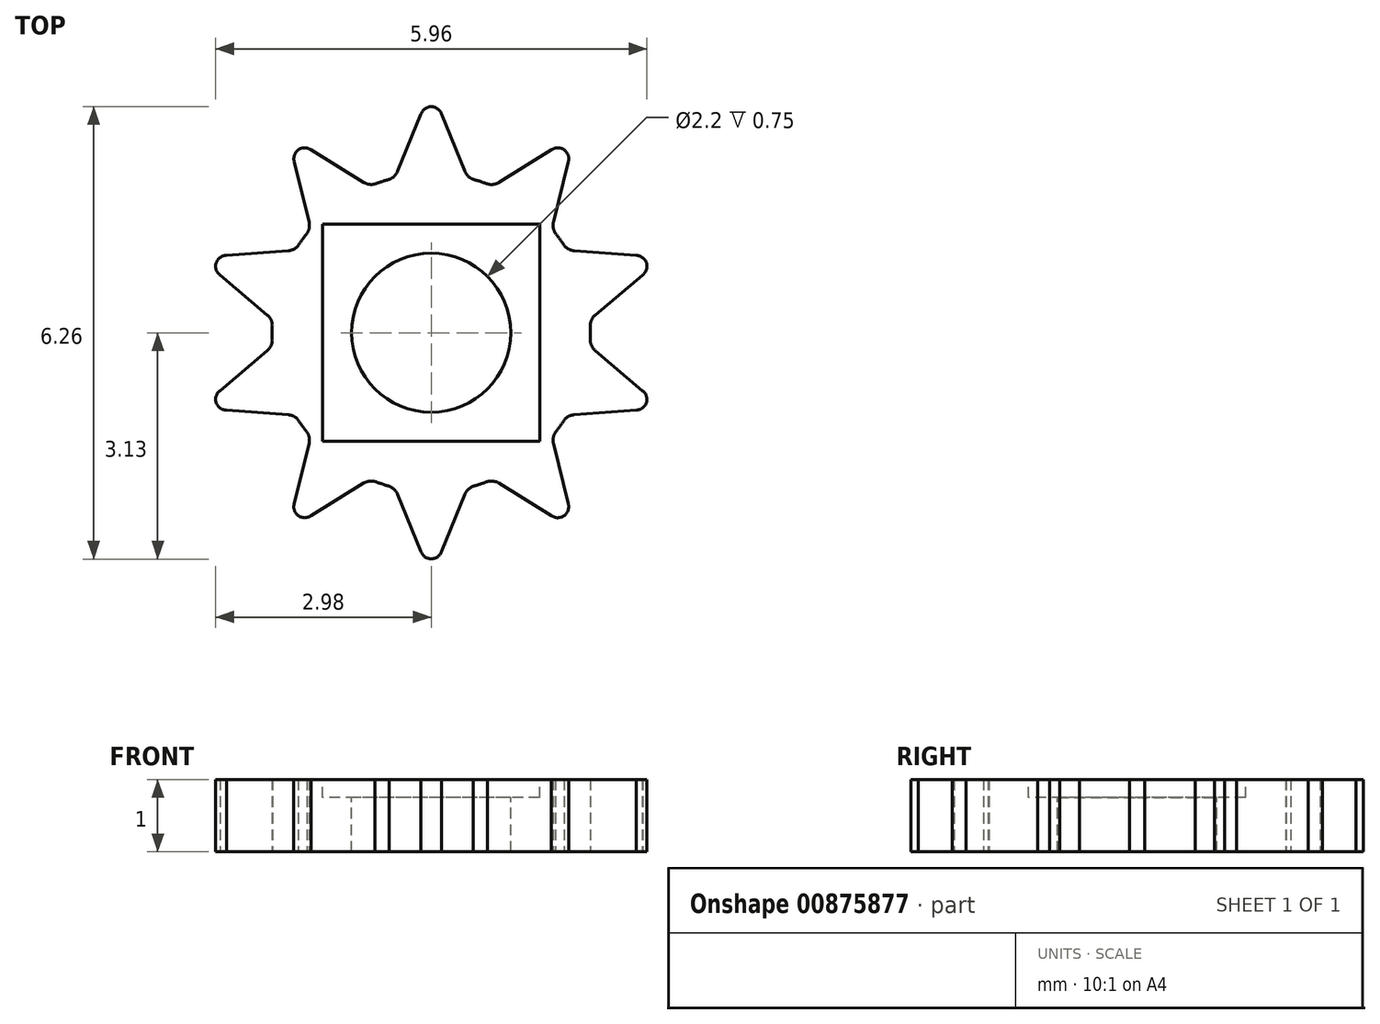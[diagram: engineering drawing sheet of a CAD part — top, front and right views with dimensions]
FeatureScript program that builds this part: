
annotation { "Feature Type Name" : "Feature", "Feature Type Description" : "" }
export const myFeature = defineFeature(function(context is Context, id is Id, definition is map)
    precondition{}
    {
        {
            var Q0;
            Q0=qCreatedBy(makeId("Top.planeOp"),FACE);
            var sketch = newSketch(context, id + "F0", { "sketchPlane" : qUnion([Q0])});
            skArc(sketch, "E0", {"start": v(-0.6, 0.8) * mm, "mid": v(0, -1) * mm, "end": v(0.6, 0.8) * mm});
            skLineSegment(sketch, "E1", {"start": v(0, 0) * mm, "end": v(0, 0.8) * mm});
            skLineSegment(sketch, "E2", {"start": v(0, 0.8) * mm, "end": v(0.6, 0.8) * mm});
            skLineSegment(sketch, "E3", {"start": v(0.6, 0.8) * mm, "end": v(-0.6, 0.8) * mm});
            skLineSegment(sketch, "E4", {"start": v(0, 0) * mm, "end": v(0, 3.13) * mm});
            skArc(sketch, "E5", {"start": v(-0.61, 2.11) * mm, "mid": v(-0.52, 2.15) * mm, "end": v(-0.47, 2.23) * mm});
            skArc(sketch, "E6", {"start": v(0.47, 2.23) * mm, "mid": v(0.52, 2.15) * mm, "end": v(0.61, 2.11) * mm});
            skLineSegment(sketch, "E7", {"start": v(0.47, 2.23) * mm, "end": v(0.14, 3.02) * mm});
            skLineSegment(sketch, "E8", {"start": v(-0.14, 3.02) * mm, "end": v(-0.47, 2.23) * mm});
            skPoint(sketch, "E9.start.orphan", {"position": v(-0.5, 4.18) * mm});
            skPoint(sketch, "E10.orphan", {"position": v(0.5, 4.18) * mm});
            skPoint(sketch, "E11.orphan", {"position": v(-0.5, 3.14) * mm});
            skPoint(sketch, "E12.orphan", {"position": v(0.5, 3.14) * mm});
            skCircle(sketch, "E13", {"center": v(0, 0) * mm, "radius": 2.2 * mm});
            skLineSegment(sketch, "E14", {"start": v(0, 2.2) * mm, "end": v(0, -0.08) * mm});
            skCircle(sketch, "E15", {"center": v(0, 2.98) * mm, "radius": 0.15 * mm});
            skLineSegment(sketch, "E16.trimOffspring", {"start": v(0, 3.18) * mm, "end": v(0, 3.18) * mm});
            skSolve(sketch);
        }
        {
            var Q0;
            Q0 = qSketchRegion(id + "F0", true);
            extrude(context, id + "F1", {"entities" : qUnion([Q0]), "depth" : 1 * mm, "offsetDistance" : 25 * mm});
        }
        {
            var Q0;
            Q0=makeQuery(id+"F1.opExtrude","SWEPT_FACE",FACE,{"disambiguationData":[OSD([sQuery(id+"F0.wireOp",EDGE,"E7")])]});
            var Q1;
            Q1=makeQuery(id+"F1.opExtrude","SWEPT_FACE",FACE,{"disambiguationData":[OSD([sQuery(id+"F0.wireOp",EDGE,"E6")])]});
            var Q2;
            Q2=makeQuery(id+"F1.opExtrude","SWEPT_FACE",FACE,{"disambiguationData":[OSD([sQuery(id+"F0.wireOp",EDGE,"E15")])]});
            var Q3;
            Q3=makeQuery(id+"F1.opExtrude","SWEPT_FACE",FACE,{"disambiguationData":[OSD([sQuery(id+"F0.wireOp",EDGE,"E8")])]});
            var Q4;
            Q4=makeQuery(id+"F1.opExtrude","SWEPT_FACE",FACE,{"disambiguationData":[OSD([sQuery(id+"F0.wireOp",EDGE,"E5")])]});
            var Q5;
            Q5=makeQuery(id+"F1.opExtrude","SWEPT_FACE",FACE,{"disambiguationData":[OSD([sQuery(id+"F0.wireOp",EDGE,"E0")])]});
            circularPattern(context, id + "F2", {"patternType" : PatternType.FACE, "faces" : qUnion([Q0, Q1, Q2, Q3, Q4]), "axis" : qUnion([Q5]), "angle" : 360 * degree, "instanceCount" : 10, "equalSpace" : true});
        }
        {
            var Q0;
            Q0=makeQuery(id+"F1.opExtrude","CAP_FACE",FACE,{"disambiguationData":[OSD([sQuery(id+"F0.wireOp",EDGE,"fvcJd2ya-tVhh-xxZW-4oz9-YDaeGeMDFEol"),sQuery(id+"F0.wireOp",EDGE,"E0"),sQuery(id+"F0.wireOp",EDGE,"E3"),sQuery(id+"F0.wireOp",EDGE,"eaARCY1Z-NOzu-Sdc5-bvnF-4fAZ0A6SJQx6"),sQuery(id+"F0.wireOp",EDGE,"E9"),sQuery(id+"F0.wireOp",EDGE,"5273f35b-b4da-4427-86f1-7bf0b3b0f4d40.MirrorCS"),sQuery(id+"F0.wireOp",EDGE,"358262c5-c650-46fa-82b1-be198478d2b90.MirrorCS")])],"isStart":false});
            var sketch = newSketch(context, id + "F3", { "sketchPlane" : qUnion([Q0])});
            skLineSegment(sketch, "E17.bottom", {"start": v(1.5, 1.5) * mm, "end": v(-1.5, 1.5) * mm});
            skLineSegment(sketch, "E17.top", {"start": v(1.5, -1.5) * mm, "end": v(-1.5, -1.5) * mm});
            skLineSegment(sketch, "E17.left", {"start": v(1.5, 1.5) * mm, "end": v(1.5, -1.5) * mm});
            skLineSegment(sketch, "E17.right", {"start": v(-1.5, 1.5) * mm, "end": v(-1.5, -1.5) * mm});
            skPoint(sketch, "E17.middle", {"position": v(0, 0) * mm});
            skSolve(sketch);
        }
        {
            var Q0;
            Q0 = qSketchRegion(id + "F3", true);
            extrude(context, id + "F4", {"entities" : qUnion([Q0]), "operationType" : NewBodyOperationType.REMOVE, "oppositeDirection" : true, "depth" : .25 * mm, "offsetDistance" : 25 * mm});
        }
        {
            var Q0;
            Q0 = qSketchRegion(id + "F0", true);
            extrude(context, id + "F5", {"entities" : qUnion([Q0]), "operationType" : NewBodyOperationType.ADD, "depth" : 1 * mm, "offsetDistance" : 25 * mm});
        }
        {
            var Q0;
            Q0=makeQuery(id+"F3.imprint","IMPRINT",FACE,{"disambiguationData":[TD([[makeQuery(id+"F3.imprint","IMPRINT",EDGE,{"derivedFrom":sQuery(id+"F3.wireOp",EDGE,"E17.bottom")}),1.0]])]});
            extrude(context, id + "F6", {"entities" : qUnion([Q0]), "operationType" : NewBodyOperationType.REMOVE, "oppositeDirection" : true, "depth" : .25 * mm, "offsetDistance" : 25 * mm});
        }
        {
            var Q0;
            Q0=makeQuery(id+"F3.imprint","IMPRINT",FACE,{"disambiguationData":[TD([[makeQuery(id+"F3.imprint","IMPRINT",EDGE,{"derivedFrom":sQuery(id+"F3.wireOp",EDGE,"E17.bottom")}),1.0]])]});
            var sketch = newSketch(context, id + "F7", { "sketchPlane" : qUnion([Q0])});
            skCircle(sketch, "E18", {"center": v(0, 0) * mm, "radius": 1.1 * mm});
            skSolve(sketch);
        }
        {
            var Q0;
            Q0 = qSketchRegion(id + "F7", true);
            extrude(context, id + "F8", {"entities" : qUnion([Q0]), "operationType" : NewBodyOperationType.REMOVE, "endBound" : BoundingType.SYMMETRIC, "oppositeDirection" : true, "depth" : 2.62 * mm, "offsetDistance" : 25 * mm});
        }
    });
